# Revit family: lgh-rn15_100rxv(d)-c_60Hz
name_source: partatom
category: 機械設備
units: mm (PartAtom-declared; Revit-internal decimal feet)

## family parameters
OmniClass タイトル = Heat Exchangers for Ventilation Air
OmniClass 番号 = 23.75.10.34.21
パーツ タイプ = 割り込み
ロード時にボイドで切り取り = いいえ
丸型コネクタ寸法 = 直径を使用
作業面ベース = いいえ
共有 = いいえ
常に垂直 = はい
部屋計算ポイント = はい

## types (14) — shared parameters
Clearance Left = 600
EAダクト変更表示 = いいえ
IfcExportAs = IfcAirToAirHeatRecoveryType
IfcExportType = ROTARYWHEEL
OAダクト変更表示 = いいえ
OmniClassCode = 23-27 23 19 11
URL = https://www.mitsubishielectric.co.jp
Uniclass2015Code = Pr_60_60_36_88
Uniclass2015Title = Thermal wheels
Uniclass2015Version = Systems v1.9
サービススペース = はい
ドレン管径 = 0 mm
仕様書バージョン = Version1.0
企業コード = 108420
分類コード = 50052504100070
初期抵抗 = 0.0 Pa
周波数 = 60 Hz
呼称 = 全熱交換ユニット
外気量 = 0.0 m³/h
実風量 = 0.0 m³/h
形名 = LGH-RN-1 : LGH-RN15-1
形式 = 天井埋込ダクト形
排気量 = 0.0 m³/h
本体マテリアル = 溶融亜鉛めっき鋼板
法定耐用年数 = 15
点検口 = はい
相 = 1
積算_科目 = 1 空気調和設備
製品リリース年月 = 2020年10月1日
製品出荷対象 = 国内
製造元 = 三菱電機株式会社
設置方法 = 天井吊(隠ぺい)形
設計風量 = 0.0 m³/h
説明 = 業務用ロスナイ 天井埋込形 DCリプレースマイコン CO2センサー付
負荷分類 = 3_ファン類
運転質量 = 0.00 kg
電動機出力 = 0 W
zero-valued in all types: Clearance Back, Clearance Bottom, Clearance Front, Clearance Right, Clearance Top, EAサイズ_W, OAサイズ_W

## per-type parameters (varying)
- LGH-RN15RXVD-C: Depth=780  [stored 2.55906 ft]; EAサイズ_D=97.5  [stored 0.319882 ft]; Height=290  [stored 0.951444 ft]; M=59; MAX静圧=180.0 Pa; MAX風量=150.0 m³/h; MID静圧=93.0 Pa; MID風量=108.0 m³/h; MIN静圧=35.0 Pa; MIN風量=66.0 m³/h; OAサイズ_D=97.5  [stored 0.319882 ft]; RAサイズ_D=97.5  [stored 0.319882 ft]; SAサイズ_D=97.5  [stored 0.319882 ft]; SMAX静圧=210.0 Pa; SMAX風量=150.0 m³/h; Width=610  [stored 2.00131 ft]; エンタルピ交換効率_冷房_弱=69.00%; エンタルピ交換効率_冷房_強=64.50%; エンタルピ交換効率_冷房_特強=64.50%; エンタルピ交換効率_暖房_弱=79.00%; エンタルピ交換効率_暖房_強=75.50%; エンタルピ交換効率_暖房_特強=75.50%; 価格=412200 $; 参照している仕様書等のバージョン=公共建築工事標準仕様書（機械設備工事編）平成31年度版; 天吊金具ピッチ奥行=768  [stored 2.51969 ft]; 天吊金具ピッチ幅=658  [stored 2.15879 ft]; 極数=3; 機外静圧=210.0 Pa; 機外静圧_排気=210.0 Pa; 消費電力=85 W; 温度交換効率_弱=78.00%; 温度交換効率_強=74.00%; 温度交換効率_特強=74.00%; 点検口高さ=-145  [stored -0.475722 ft]; 製品質量=23.00 kg; 質量=27.60 kg; 電圧=200 V; 面風速=5.3 m/s; 風量=150.0 m³/h; 騒音レベル(dB(A))=31
- LGH-RN25RXVD-C: Depth=780  [stored 2.55906 ft]; EAサイズ_D=142  [stored 0.465879 ft]; Height=290  [stored 0.951444 ft]; M=69  [stored 0.226378 ft]; MAX静圧=145.0 Pa; MAX風量=250.0 m³/h; MID静圧=75.0 Pa; MID風量=180.0 m³/h; MIN静圧=28.0 Pa; MIN風量=110.0 m³/h; OAサイズ_D=142  [stored 0.465879 ft]; RAサイズ_D=142  [stored 0.465879 ft]; SAサイズ_D=142  [stored 0.465879 ft]; SMAX静圧=170.0 Pa; SMAX風量=250.0 m³/h; Width=735; エンタルピ交換効率_冷房_弱=68.50%; エンタルピ交換効率_冷房_強=63.00%; エンタルピ交換効率_冷房_特強=63.00%; エンタルピ交換効率_暖房_弱=78.50%; エンタルピ交換効率_暖房_強=73.00%; エンタルピ交換効率_暖房_特強=73.00%; 価格=433200 $; 参照している仕様書等のバージョン=公共建築工事標準仕様書（機械設備工事編）平成31年度版; 天吊金具ピッチ奥行=768  [stored 2.51969 ft]; 天吊金具ピッチ幅=782; 極数=3; 機外静圧=170.0 Pa; 機外静圧_排気=170.0 Pa; 消費電力=110 W; 温度交換効率_弱=78.00%; 温度交換効率_強=70.00%; 温度交換効率_特強=70.00%; 点検口高さ=-145  [stored -0.475722 ft]; 製品質量=24.00 kg; 質量=28.80 kg; 電圧=200 V; 面風速=3.9 m/s; 風量=250.0 m³/h; 騒音レベル(dB(A))=30
- LGH-RN35RXVD-C: Depth=890  [stored 2.91995 ft]; EAサイズ_D=142  [stored 0.465879 ft]; Height=330; M=69  [stored 0.226378 ft]; MAX静圧=185.0 Pa; MAX風量=350.0 m³/h; MID静圧=96.0 Pa; MID風量=252.0 m³/h; MIN静圧=36.0 Pa; MIN風量=154.0 m³/h; OAサイズ_D=142  [stored 0.465879 ft]; RAサイズ_D=142  [stored 0.465879 ft]; SAサイズ_D=142  [stored 0.465879 ft]; SMAX静圧=300.0 Pa; SMAX風量=350.0 m³/h; Width=875  [stored 2.87073 ft]; エンタルピ交換効率_冷房_弱=66.50%; エンタルピ交換効率_冷房_強=65.50%; エンタルピ交換効率_冷房_特強=65.50%; エンタルピ交換効率_暖房_弱=78.50%; エンタルピ交換効率_暖房_強=74.50%; エンタルピ交換効率_暖房_特強=74.50%; 価格=458200 $; 参照している仕様書等のバージョン=公共建築工事標準仕様書（機械設備工事編）平成31年度版; 天吊金具ピッチ奥行=875  [stored 2.87073 ft]; 天吊金具ピッチ幅=921  [stored 3.02165 ft]; 極数=3; 機外静圧=300.0 Pa; 機外静圧_排気=300.0 Pa; 消費電力=210 W; 温度交換効率_弱=75.00%; 温度交換効率_強=71.50%; 温度交換効率_特強=71.50%; 点検口高さ=-165  [stored -0.541339 ft]; 製品質量=33.00 kg; 質量=39.60 kg; 電圧=200 V; 面風速=5.5 m/s; 風量=350.0 m³/h; 騒音レベル(dB(A))=33
- LGH-RN50RXVD-C: Depth=890  [stored 2.91995 ft]; EAサイズ_D=192  [stored 0.629921 ft]; Height=330; M=84  [stored 0.275591 ft]; MAX静圧=190.0 Pa; MAX風量=500.0 m³/h; MID静圧=98.0 Pa; MID風量=360.0 m³/h; MIN静圧=37.0 Pa; MIN風量=220.0 m³/h; OAサイズ_D=192  [stored 0.629921 ft]; RAサイズ_D=192  [stored 0.629921 ft]; SAサイズ_D=192  [stored 0.629921 ft]; SMAX静圧=310.0 Pa; SMAX風量=500.0 m³/h; Width=1020  [stored 3.34646 ft]; エンタルピ交換効率_冷房_弱=66.50%; エンタルピ交換効率_冷房_強=63.00%; エンタルピ交換効率_冷房_特強=63.00%; エンタルピ交換効率_暖房_弱=77.50%; エンタルピ交換効率_暖房_強=73.00%; エンタルピ交換効率_暖房_特強=73.00%; 価格=519200 $; 参照している仕様書等のバージョン=公共建築工事標準仕様書（機械設備工事編）平成31年度版; 天吊金具ピッチ奥行=875  [stored 2.87073 ft]; 天吊金具ピッチ幅=1063; 極数=3; 機外静圧=310.0 Pa; 機外静圧_排気=310.0 Pa; 消費電力=315 W; 温度交換効率_弱=75.00%; 温度交換効率_強=71.00%; 温度交換効率_特強=71.00%; 点検口高さ=-165  [stored -0.541339 ft]; 製品質量=37.00 kg; 質量=44.40 kg; 電圧=200 V; 面風速=4.4 m/s; 風量=500.0 m³/h; 騒音レベル(dB(A))=37
- LGH-RN65RXVD-C: Depth=984  [stored 3.22835 ft]; EAサイズ_D=192  [stored 0.629921 ft]; Height=404  [stored 1.32546 ft]; M=84  [stored 0.275591 ft]; MAX静圧=230.0 Pa; MAX風量=650.0 m³/h; MID静圧=119.0 Pa; MID風量=468.0 m³/h; MIN静圧=45.0 Pa; MIN風量=286.0 m³/h; OAサイズ_D=192  [stored 0.629921 ft]; RAサイズ_D=192  [stored 0.629921 ft]; SAサイズ_D=192  [stored 0.629921 ft]; SMAX静圧=320.0 Pa; SMAX風量=650.0 m³/h; Width=892  [stored 2.92651 ft]; エンタルピ交換効率_冷房_弱=67.00%; エンタルピ交換効率_冷房_強=63.00%; エンタルピ交換効率_冷房_特強=63.00%; エンタルピ交換効率_暖房_弱=76.00%; エンタルピ交換効率_暖房_強=72.00%; エンタルピ交換効率_暖房_特強=72.00%; 価格=629200 $; 参照している仕様書等のバージョン=公共建築工事標準仕様書（機械設備工事編）平成31年度版; 天吊金具ピッチ奥行=895  [stored 2.93635 ft]; 天吊金具ピッチ幅=1001  [stored 3.28412 ft]; 極数=3; 機外静圧=320.0 Pa; 機外静圧_排気=320.0 Pa; 消費電力=445 W; 温度交換効率_弱=76.00%; 温度交換効率_強=71.50%; 温度交換効率_特強=71.50%; 点検口高さ=-202  [stored -0.66273 ft]; 製品質量=43.00 kg; 質量=51.60 kg; 電圧=200 V; 面風速=5.8 m/s; 風量=650.0 m³/h; 騒音レベル(dB(A))=40
- LGH-RN80RXVD-C: Depth=1144; EAサイズ_D=242  [stored 0.793963 ft]; Height=404  [stored 1.32546 ft]; M=84  [stored 0.275591 ft]; MAX静圧=190.0 Pa; MAX風量=800.0 m³/h; MID静圧=98.0 Pa; MID風量=576.0 m³/h; MIN静圧=37.0 Pa; MIN風量=352.0 m³/h; OAサイズ_D=242  [stored 0.793963 ft]; RAサイズ_D=242  [stored 0.793963 ft]; SAサイズ_D=242  [stored 0.793963 ft]; SMAX静圧=310.0 Pa; SMAX風量=800.0 m³/h; Width=1004  [stored 3.29396 ft]; エンタルピ交換効率_冷房_弱=68.00%; エンタルピ交換効率_冷房_強=65.00%; エンタルピ交換効率_冷房_特強=65.00%; エンタルピ交換効率_暖房_弱=78.00%; エンタルピ交換効率_暖房_強=75.00%; エンタルピ交換効率_暖房_特強=75.00%; 価格=713200 $; 参照している仕様書等のバージョン=公共建築工事標準仕様書（機械設備工事編）平成31年度版; 天吊金具ピッチ奥行=1131  [stored 3.71063 ft]; 天吊金具ピッチ幅=1051  [stored 3.44816 ft]; 極数=3; 機外静圧=310.0 Pa; 機外静圧_排気=310.0 Pa; 消費電力=540 W; 温度交換効率_弱=76.50%; 温度交換効率_強=73.00%; 温度交換効率_特強=73.00%; 点検口高さ=-202  [stored -0.66273 ft]; 製品質量=53.00 kg; 質量=63.60 kg; 電圧=200 V; 面風速=4.5 m/s; 風量=800.0 m³/h; 騒音レベル(dB(A))=40
- LGH-RN100RXVD-C: Depth=1144; EAサイズ_D=242  [stored 0.793963 ft]; Height=404  [stored 1.32546 ft]; M=84  [stored 0.275591 ft]; MAX静圧=165.0 Pa; MAX風量=1000.0 m³/h; MID静圧=86.0 Pa; MID風量=720.0 m³/h; MIN静圧=32.0 Pa; MIN風量=440.0 m³/h; OAサイズ_D=242  [stored 0.793963 ft]; RAサイズ_D=242  [stored 0.793963 ft]; SAサイズ_D=242  [stored 0.793963 ft]; SMAX静圧=225.0 Pa; SMAX風量=1000.0 m³/h; Width=1231  [stored 4.03871 ft]; エンタルピ交換効率_冷房_弱=67.50%; エンタルピ交換効率_冷房_強=65.00%; エンタルピ交換効率_冷房_特強=65.00%; エンタルピ交換効率_暖房_弱=76.50%; エンタルピ交換効率_暖房_強=75.00%; エンタルピ交換効率_暖房_特強=75.00%; 価格=785200 $; 天吊金具ピッチ奥行=1131  [stored 3.71063 ft]; 天吊金具ピッチ幅=1278  [stored 4.19291 ft]; 極数=3; 機外静圧=225.0 Pa; 機外静圧_排気=225.0 Pa; 消費電力=580 W; 温度交換効率_弱=75.00%; 温度交換効率_強=73.00%; 温度交換効率_特強=73.00%; 点検口高さ=-202  [stored -0.66273 ft]; 製品質量=58.00 kg; 質量=69.60 kg; 電圧=200 V; 面風速=5.7 m/s; 風量=1000.0 m³/h; 騒音レベル(dB(A))=38
- LGH-RN15RXV-C: Depth=780  [stored 2.55906 ft]; EAサイズ_D=97.5  [stored 0.319882 ft]; Height=290  [stored 0.951444 ft]; M=59; MAX静圧=180.0 Pa; MAX風量=150.0 m³/h; MID静圧=93.0 Pa; MID風量=108.0 m³/h; MIN静圧=35.0 Pa; MIN風量=66.0 m³/h; OAサイズ_D=97.5  [stored 0.319882 ft]; RAサイズ_D=97.5  [stored 0.319882 ft]; SAサイズ_D=97.5  [stored 0.319882 ft]; SMAX静圧=210.0 Pa; SMAX風量=150.0 m³/h; Width=610  [stored 2.00131 ft]; エンタルピ交換効率_冷房_弱=69.00%; エンタルピ交換効率_冷房_強=64.50%; エンタルピ交換効率_冷房_特強=64.50%; エンタルピ交換効率_暖房_弱=79.00%; エンタルピ交換効率_暖房_強=75.50%; エンタルピ交換効率_暖房_特強=75.50%; 価格=412200 $; 参照している仕様書等のバージョン=公共建築工事標準仕様書（機械設備工事編）平成31年度版; 天吊金具ピッチ奥行=768  [stored 2.51969 ft]; 天吊金具ピッチ幅=658  [stored 2.15879 ft]; 極数=2; 機外静圧=210.0 Pa; 機外静圧_排気=210.0 Pa; 消費電力=85 W; 温度交換効率_弱=78.00%; 温度交換効率_強=74.00%; 温度交換効率_特強=74.00%; 点検口高さ=-145  [stored -0.475722 ft]; 製品質量=23.00 kg; 質量=27.60 kg; 電圧=100 V; 面風速=5.3 m/s; 風量=150.0 m³/h; 騒音レベル(dB(A))=31
- LGH-RN25RXV-C: Depth=780  [stored 2.55906 ft]; EAサイズ_D=142  [stored 0.465879 ft]; Height=290  [stored 0.951444 ft]; M=69  [stored 0.226378 ft]; MAX静圧=145.0 Pa; MAX風量=250.0 m³/h; MID静圧=75.0 Pa; MID風量=180.0 m³/h; MIN静圧=28.0 Pa; MIN風量=110.0 m³/h; OAサイズ_D=142  [stored 0.465879 ft]; RAサイズ_D=142  [stored 0.465879 ft]; SAサイズ_D=142  [stored 0.465879 ft]; SMAX静圧=170.0 Pa; SMAX風量=250.0 m³/h; Width=735; エンタルピ交換効率_冷房_弱=68.50%; エンタルピ交換効率_冷房_強=63.00%; エンタルピ交換効率_冷房_特強=63.00%; エンタルピ交換効率_暖房_弱=78.50%; エンタルピ交換効率_暖房_強=73.00%; エンタルピ交換効率_暖房_特強=73.00%; 価格=433200 $; 参照している仕様書等のバージョン=公共建築工事標準仕様書（機械設備工事編）平成31年度版; 天吊金具ピッチ奥行=768  [stored 2.51969 ft]; 天吊金具ピッチ幅=782; 極数=2; 機外静圧=170.0 Pa; 機外静圧_排気=170.0 Pa; 消費電力=110 W; 温度交換効率_弱=78.00%; 温度交換効率_強=70.00%; 温度交換効率_特強=70.00%; 点検口高さ=-145  [stored -0.475722 ft]; 製品質量=24.00 kg; 質量=28.80 kg; 電圧=100 V; 面風速=3.9 m/s; 風量=250.0 m³/h; 騒音レベル(dB(A))=30
- LGH-RN35RXV-C: Depth=890  [stored 2.91995 ft]; EAサイズ_D=142  [stored 0.465879 ft]; Height=330; M=69  [stored 0.226378 ft]; MAX静圧=185.0 Pa; MAX風量=350.0 m³/h; MID静圧=96.0 Pa; MID風量=252.0 m³/h; MIN静圧=36.0 Pa; MIN風量=154.0 m³/h; OAサイズ_D=142  [stored 0.465879 ft]; RAサイズ_D=142  [stored 0.465879 ft]; SAサイズ_D=142  [stored 0.465879 ft]; SMAX静圧=300.0 Pa; SMAX風量=350.0 m³/h; Width=875  [stored 2.87073 ft]; エンタルピ交換効率_冷房_弱=66.50%; エンタルピ交換効率_冷房_強=65.50%; エンタルピ交換効率_冷房_特強=65.50%; エンタルピ交換効率_暖房_弱=78.50%; エンタルピ交換効率_暖房_強=74.50%; エンタルピ交換効率_暖房_特強=74.50%; 価格=458200 $; 参照している仕様書等のバージョン=公共建築工事標準仕様書（機械設備工事編）平成31年度版; 天吊金具ピッチ奥行=875  [stored 2.87073 ft]; 天吊金具ピッチ幅=921  [stored 3.02165 ft]; 極数=2; 機外静圧=300.0 Pa; 機外静圧_排気=300.0 Pa; 消費電力=210 W; 温度交換効率_弱=75.00%; 温度交換効率_強=71.50%; 温度交換効率_特強=71.50%; 点検口高さ=-165  [stored -0.541339 ft]; 製品質量=33.00 kg; 質量=39.60 kg; 電圧=100 V; 面風速=5.5 m/s; 風量=350.0 m³/h; 騒音レベル(dB(A))=33
- LGH-RN50RXV-C: Depth=890  [stored 2.91995 ft]; EAサイズ_D=192  [stored 0.629921 ft]; Height=330; M=84  [stored 0.275591 ft]; MAX静圧=190.0 Pa; MAX風量=500.0 m³/h; MID静圧=98.0 Pa; MID風量=360.0 m³/h; MIN静圧=37.0 Pa; MIN風量=220.0 m³/h; OAサイズ_D=192  [stored 0.629921 ft]; RAサイズ_D=192  [stored 0.629921 ft]; SAサイズ_D=192  [stored 0.629921 ft]; SMAX静圧=310.0 Pa; SMAX風量=500.0 m³/h; Width=1020  [stored 3.34646 ft]; エンタルピ交換効率_冷房_弱=66.50%; エンタルピ交換効率_冷房_強=63.00%; エンタルピ交換効率_冷房_特強=63.00%; エンタルピ交換効率_暖房_弱=77.50%; エンタルピ交換効率_暖房_強=73.00%; エンタルピ交換効率_暖房_特強=73.00%; 価格=519200 $; 参照している仕様書等のバージョン=公共建築工事標準仕様書（機械設備工事編）平成31年度版; 天吊金具ピッチ奥行=875  [stored 2.87073 ft]; 天吊金具ピッチ幅=1063; 極数=2; 機外静圧=310.0 Pa; 機外静圧_排気=310.0 Pa; 消費電力=315 W; 温度交換効率_弱=75.00%; 温度交換効率_強=71.00%; 温度交換効率_特強=71.00%; 点検口高さ=-165  [stored -0.541339 ft]; 製品質量=37.00 kg; 質量=44.40 kg; 電圧=100 V; 面風速=4.4 m/s; 風量=500.0 m³/h; 騒音レベル(dB(A))=37
- LGH-RN65RXV-C: Depth=984  [stored 3.22835 ft]; EAサイズ_D=192  [stored 0.629921 ft]; Height=404  [stored 1.32546 ft]; M=84  [stored 0.275591 ft]; MAX静圧=230.0 Pa; MAX風量=650.0 m³/h; MID静圧=119.0 Pa; MID風量=468.0 m³/h; MIN静圧=45.0 Pa; MIN風量=286.0 m³/h; OAサイズ_D=192  [stored 0.629921 ft]; RAサイズ_D=192  [stored 0.629921 ft]; SAサイズ_D=192  [stored 0.629921 ft]; SMAX静圧=320.0 Pa; SMAX風量=650.0 m³/h; Width=892  [stored 2.92651 ft]; エンタルピ交換効率_冷房_弱=67.00%; エンタルピ交換効率_冷房_強=63.00%; エンタルピ交換効率_冷房_特強=63.00%; エンタルピ交換効率_暖房_弱=76.00%; エンタルピ交換効率_暖房_強=72.00%; エンタルピ交換効率_暖房_特強=72.00%; 価格=629200 $; 参照している仕様書等のバージョン=公共建築工事標準仕様書（機械設備工事編）平成31年度版; 天吊金具ピッチ奥行=895  [stored 2.93635 ft]; 天吊金具ピッチ幅=1001  [stored 3.28412 ft]; 極数=2; 機外静圧=320.0 Pa; 機外静圧_排気=320.0 Pa; 消費電力=445 W; 温度交換効率_弱=76.00%; 温度交換効率_強=71.50%; 温度交換効率_特強=71.50%; 点検口高さ=-202  [stored -0.66273 ft]; 製品質量=43.00 kg; 質量=51.60 kg; 電圧=100 V; 面風速=5.8 m/s; 風量=650.0 m³/h; 騒音レベル(dB(A))=40
- LGH-RN80RXV-C: Depth=1144; EAサイズ_D=242  [stored 0.793963 ft]; Height=404  [stored 1.32546 ft]; M=84  [stored 0.275591 ft]; MAX静圧=190.0 Pa; MAX風量=800.0 m³/h; MID静圧=98.0 Pa; MID風量=576.0 m³/h; MIN静圧=37.0 Pa; MIN風量=352.0 m³/h; OAサイズ_D=242  [stored 0.793963 ft]; RAサイズ_D=242  [stored 0.793963 ft]; SAサイズ_D=242  [stored 0.793963 ft]; SMAX静圧=310.0 Pa; SMAX風量=800.0 m³/h; Width=1004  [stored 3.29396 ft]; エンタルピ交換効率_冷房_弱=68.00%; エンタルピ交換効率_冷房_強=65.00%; エンタルピ交換効率_冷房_特強=65.00%; エンタルピ交換効率_暖房_弱=78.00%; エンタルピ交換効率_暖房_強=75.00%; エンタルピ交換効率_暖房_特強=75.00%; 価格=713200 $; 参照している仕様書等のバージョン=公共建築工事標準仕様書（機械設備工事編）平成31年度版; 天吊金具ピッチ奥行=1131  [stored 3.71063 ft]; 天吊金具ピッチ幅=1051  [stored 3.44816 ft]; 極数=2; 機外静圧=310.0 Pa; 機外静圧_排気=310.0 Pa; 消費電力=540 W; 温度交換効率_弱=76.50%; 温度交換効率_強=73.00%; 温度交換効率_特強=73.00%; 点検口高さ=-202  [stored -0.66273 ft]; 製品質量=53.00 kg; 質量=63.60 kg; 電圧=100 V; 面風速=4.5 m/s; 風量=800.0 m³/h; 騒音レベル(dB(A))=40
- LGH-RN100RXV-C: Depth=1144; EAサイズ_D=242  [stored 0.793963 ft]; Height=404  [stored 1.32546 ft]; M=84  [stored 0.275591 ft]; MAX静圧=165.0 Pa; MAX風量=1000.0 m³/h; MID静圧=86.0 Pa; MID風量=720.0 m³/h; MIN静圧=32.0 Pa; MIN風量=440.0 m³/h; OAサイズ_D=242  [stored 0.793963 ft]; RAサイズ_D=242  [stored 0.793963 ft]; SAサイズ_D=242  [stored 0.793963 ft]; SMAX静圧=225.0 Pa; SMAX風量=1000.0 m³/h; Width=1231  [stored 4.03871 ft]; エンタルピ交換効率_冷房_弱=67.50%; エンタルピ交換効率_冷房_強=65.00%; エンタルピ交換効率_冷房_特強=65.00%; エンタルピ交換効率_暖房_弱=76.50%; エンタルピ交換効率_暖房_強=75.00%; エンタルピ交換効率_暖房_特強=75.00%; 価格=785200 $; 天吊金具ピッチ奥行=1131  [stored 3.71063 ft]; 天吊金具ピッチ幅=1278  [stored 4.19291 ft]; 極数=2; 機外静圧=225.0 Pa; 機外静圧_排気=225.0 Pa; 消費電力=580 W; 温度交換効率_弱=75.00%; 温度交換効率_強=73.00%; 温度交換効率_特強=73.00%; 点検口高さ=-202  [stored -0.66273 ft]; 製品質量=58.00 kg; 質量=69.60 kg; 電圧=100 V; 面風速=5.7 m/s; 風量=1000.0 m³/h; 騒音レベル(dB(A))=38

note: column(s) folded — value = type name in every type: モデル

note: [stored X ft] marks values corroborated as IEEE doubles in the binary element streams (Revit-internal decimal feet)
